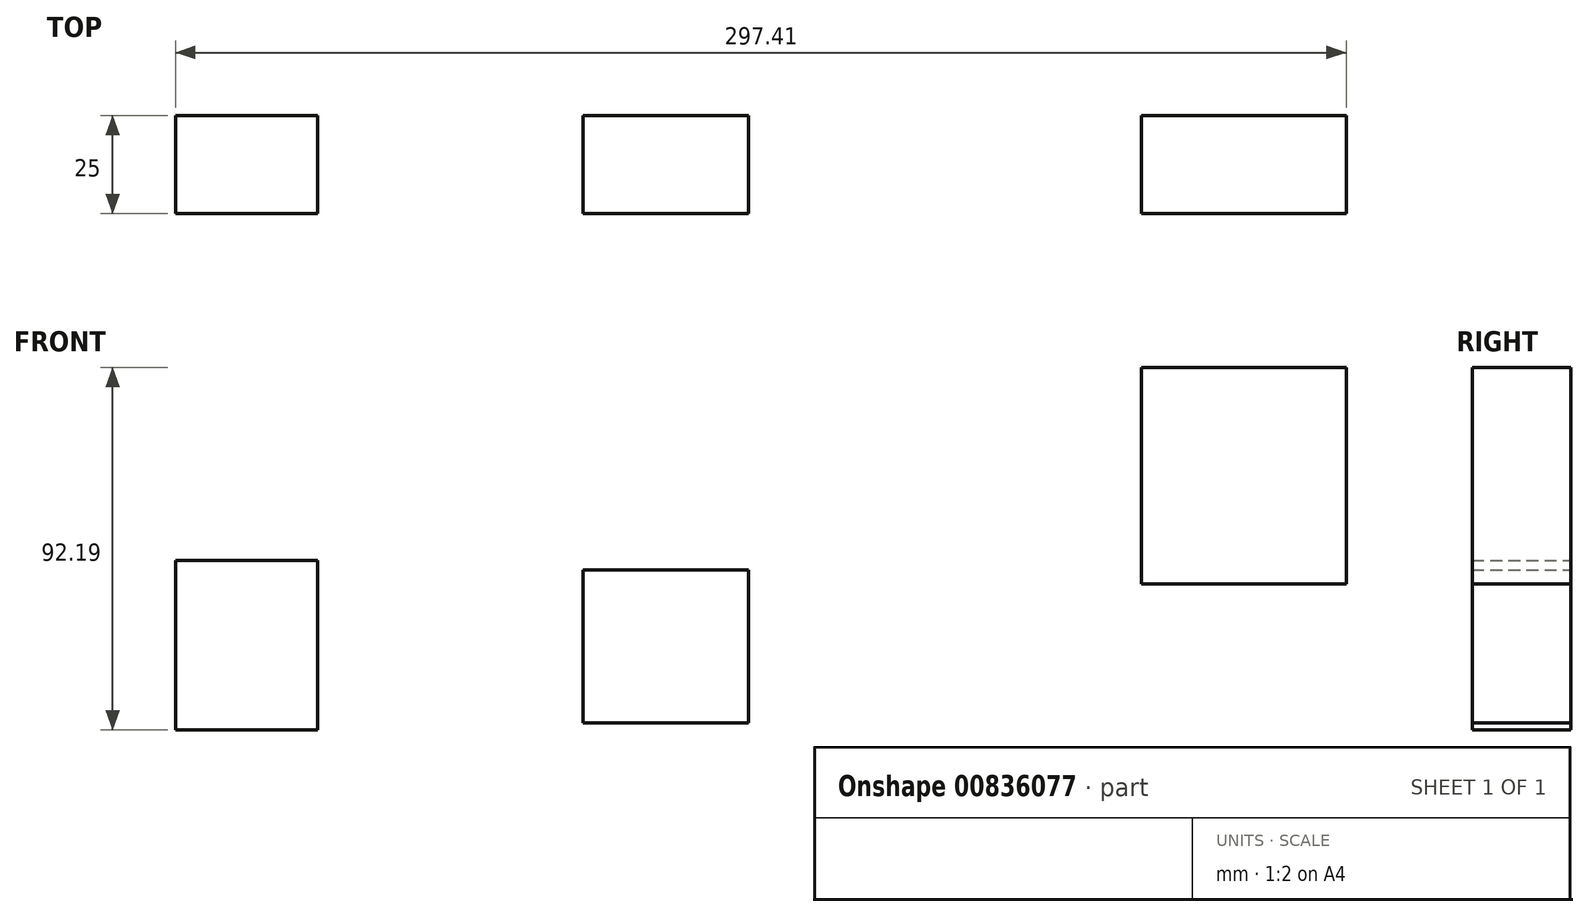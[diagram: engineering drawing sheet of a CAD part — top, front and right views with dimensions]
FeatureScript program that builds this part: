
annotation { "Feature Type Name" : "Feature", "Feature Type Description" : "" }
export const myFeature = defineFeature(function(context is Context, id is Id, definition is map)
    precondition{}
    {
        {
            var Q0;
            Q0=qCreatedBy(makeId("Front.planeOp"),FACE);
            var sketch = newSketch(context, id + "F0", { "sketchPlane" : qUnion([Q0])});
            skLineSegment(sketch, "E0.bottom", {"start": v(-178.4, 6.08) * mm, "end": v(-142.36, 6.08) * mm});
            skLineSegment(sketch, "E0.top", {"start": v(-178.4, 49.2) * mm, "end": v(-142.36, 49.2) * mm});
            skLineSegment(sketch, "E0.left", {"start": v(-178.4, 6.08) * mm, "end": v(-178.4, 49.2) * mm});
            skLineSegment(sketch, "E0.right", {"start": v(-142.36, 6.08) * mm, "end": v(-142.36, 49.2) * mm});
            skPoint(sketch, "E0.middle", {"position": v(-160.38, 27.63) * mm});
            skLineSegment(sketch, "E1.bottom", {"start": v(-74.94, 7.9) * mm, "end": v(-32.88, 7.9) * mm});
            skLineSegment(sketch, "E1.top", {"start": v(-74.94, 46.75) * mm, "end": v(-32.88, 46.75) * mm});
            skLineSegment(sketch, "E1.left", {"start": v(-74.94, 7.9) * mm, "end": v(-74.94, 46.75) * mm});
            skLineSegment(sketch, "E1.right", {"start": v(-32.88, 7.9) * mm, "end": v(-32.88, 46.75) * mm});
            skPoint(sketch, "E1.middle", {"position": v(-53.9, 27.33) * mm});
            skLineSegment(sketch, "E2.bottom", {"start": v(66.92, 43.19) * mm, "end": v(119, 43.19) * mm});
            skLineSegment(sketch, "E2.top", {"start": v(66.92, 98.27) * mm, "end": v(119, 98.27) * mm});
            skLineSegment(sketch, "E2.left", {"start": v(66.92, 43.19) * mm, "end": v(66.92, 98.27) * mm});
            skLineSegment(sketch, "E2.right", {"start": v(119, 43.19) * mm, "end": v(119, 98.27) * mm});
            skPoint(sketch, "E2.middle", {"position": v(92.96, 70.73) * mm});
            skSolve(sketch);
        }
        {
            var Q0;
            Q0=makeQuery(id+"F0.imprint","IMPRINT",FACE,{"disambiguationData":[TD([[makeQuery(id+"F0.imprint","IMPRINT",EDGE,{"derivedFrom":sQuery(id+"F0.wireOp",EDGE,"E1.bottom")}),1.0]])]});
            var Q1;
            Q1=makeQuery(id+"F0.imprint","IMPRINT",FACE,{"disambiguationData":[TD([[makeQuery(id+"F0.imprint","IMPRINT",EDGE,{"derivedFrom":sQuery(id+"F0.wireOp",EDGE,"E2.bottom")}),1.0]])]});
            var Q2;
            Q2=makeQuery(id+"F0.imprint","IMPRINT",FACE,{"disambiguationData":[TD([[makeQuery(id+"F0.imprint","IMPRINT",EDGE,{"derivedFrom":sQuery(id+"F0.wireOp",EDGE,"E0.bottom")}),1.0]])]});
            extrude(context, id + "F1", {"entities" : qUnion([Q0, Q1, Q2]), "depth" : 25 * mm, "offsetDistance" : 25 * mm});
        }
    });
